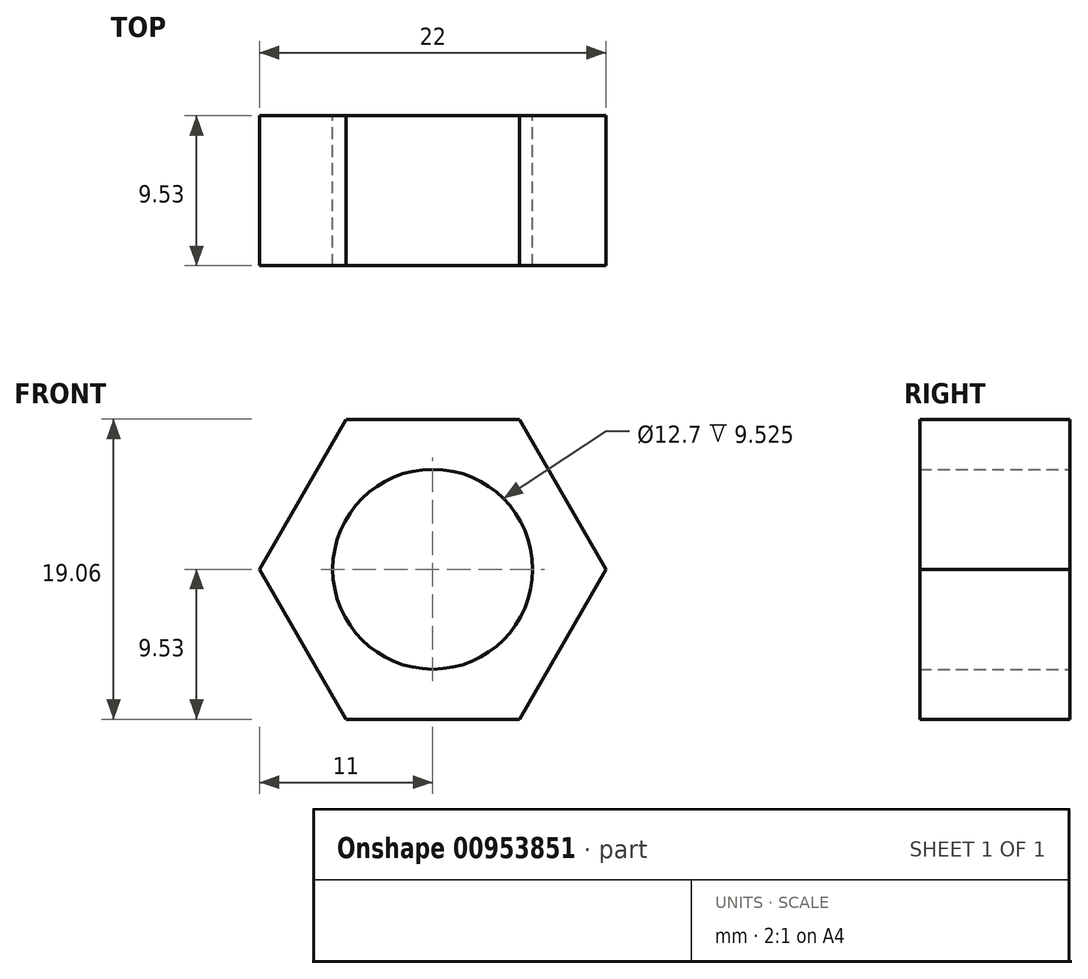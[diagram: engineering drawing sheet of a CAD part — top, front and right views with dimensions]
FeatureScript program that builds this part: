
annotation { "Feature Type Name" : "Feature", "Feature Type Description" : "" }
export const myFeature = defineFeature(function(context is Context, id is Id, definition is map)
    precondition{}
    {
        {
            var Q0;
            Q0=qCreatedBy(makeId("Front.planeOp"),FACE);
            var sketch = newSketch(context, id + "F0", { "sketchPlane" : qUnion([Q0])});
            skCircle(sketch, "E0.cCircle", {"center": v(0, 0) * mm, "radius": 9.53 * mm, "construction": true});
            skLineSegment(sketch, "E0.0", {"start": v(-5.5, 9.53) * mm, "end": v(5.5, 9.53) * mm});
            skLineSegment(sketch, "E0.1", {"start": v(5.5, 9.53) * mm, "end": v(11, 0) * mm});
            skLineSegment(sketch, "E0.2", {"start": v(11, 0) * mm, "end": v(5.5, -9.52) * mm});
            skLineSegment(sketch, "E0.3", {"start": v(5.5, -9.52) * mm, "end": v(-5.5, -9.53) * mm});
            skLineSegment(sketch, "E0.4", {"start": v(-5.5, -9.53) * mm, "end": v(-11, 0) * mm});
            skLineSegment(sketch, "E0.5", {"start": v(-11, 0) * mm, "end": v(-5.5, 9.52) * mm});
            skPoint(sketch, "E0.0.midPoint", {"position": v(0, 9.53) * mm});
            skCircle(sketch, "E1", {"center": v(0, 0) * mm, "radius": 6.35 * mm});
            skSolve(sketch);
        }
        {
            var Q0;
            Q0 = qSketchRegion(id + "F0", true);
            extrude(context, id + "F1", {"entities" : qUnion([Q0]), "depth" : 9.52 * mm, "offsetDistance" : 25.4 * mm});
        }
    });
